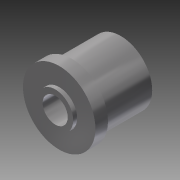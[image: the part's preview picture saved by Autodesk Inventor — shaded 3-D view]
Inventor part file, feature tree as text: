
AUTODESK INVENTOR PART (.ipt)
format: ipt  version: 2014 (Build 180170000, 170)  size: 126,976 bytes
history: native  units: mm
features: extrude x4, sketch x4
ambient origin geometry x8: Origin, YZ Plane, XZ Plane, XY Plane, X Axis, Y Axis, Z Axis, Center Point
bodies: Solid1 (feature_tree)
feature tree (8):
  extrude  "Extrusion1"  Depth=4.4mm
  extrude  "Extrusion2"  Depth=0.7mm
  extrude  "Extrusion3"  Depth=2.2mm
  extrude  "Extrusion4"  Depth=0.7mm TaperAngle=0.0deg
  sketch  "Sketch1"  dims[d0=6.3mm d1=4.4mm]
  sketch  "Sketch2"  dims[d2=0.7mm d3=0.0mm d4=12.7mm]
  sketch  "Sketch3"  dims[d5=2.2mm d6=0.0mm d7=11.0mm]
  sketch  "Sketch4"  dims[d8=8.6mm d9=0.0mm d10=0.7mm d11=0.0mm]
